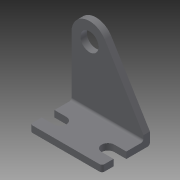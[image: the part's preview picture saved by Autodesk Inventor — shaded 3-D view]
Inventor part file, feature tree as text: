
AUTODESK INVENTOR PART (.ipt)
format: ipt  version: 2014 (Build 180170000, 170)  size: 189,440 bytes
history: native  units: in
note: dims shown in document units (in); Inventor stores cm internally (conversion verified against a paired STEP export)
features: other x147, sketch x8, extrude x5, hole x3
ambient origin geometry x8: Origin, YZ Plane, XZ Plane, XY Plane, X Axis, Y Axis, Z Axis, Center Point
bodies: Solid1 (feature_tree)
feature tree (163):
  extrude  "Extrusion1"  Depth=1.0in TaperAngle=0.0deg
  extrude  "Extrusion2"  Depth=0.1345in TaperAngle=0.0deg
  hole  "Hole1"  [1 undecoded]
  hole  "Hole2"  [1 undecoded]
  hole  "Hole3"  [1 undecoded]
  sketch  "Sketch_6"
  sketch  "Sketch_7"
  extrude  "Extrusion3"  [1 undecoded]
  extrude  "Extrusion4"  [1 undecoded]
  extrude  "Extrusion5"  [1 undecoded]
  other  "a1_XY"
  other  "a1_YZ"
  other  "a1_ZX"
  other  "a1_X"
  other  "a1_Y"
  other  "a1_Z"
  other  "a1_Center"
  other  "a2_XY"
  other  "a2_YZ"
  other  "a2_ZX"
  other  "a2_X"
  other  "a2_Y"
  other  "a2_Z"
  other  "a2_Center"
  other  "b1_XY"
  other  "b1_YZ"
  other  "b1_ZX"
  other  "b1_X"
  other  "b1_Y"
  other  "b1_Z"
  other  "b1_Center"
  other  "b2_XY"
  other  "b2_YZ"
  other  "b2_ZX"
  other  "b2_X"
  other  "b2_Y"
  other  "b2_Z"
  other  "b2_Center"
  other  "d1_XY"
  other  "d1_YZ"
  other  "d1_ZX"
  other  "d1_X"
  other  "d1_Y"
  other  "d1_Z"
  other  "d1_Center"
  other  "d2_XY"
  other  "d2_YZ"
  other  "d2_ZX"
  other  "d2_X"
  other  "d2_Y"
  other  "d2_Z"
  other  "d2_Center"
  other  "e1_XY"
  other  "e1_YZ"
  other  "e1_ZX"
  other  "e1_X"
  other  "e1_Y"
  other  "e1_Z"
  other  "e1_Center"
  other  "e2_XY"
  other  "e2_YZ"
  other  "e2_ZX"
  other  "e2_X"
  other  "e2_Y"
  other  "e2_Z"
  other  "e2_Center"
  other  "f1_XY"
  other  "f1_YZ"
  other  "f1_ZX"
  other  "f1_X"
  other  "f1_Y"
  other  "f1_Z"
  other  "f1_Center"
  other  "f2_XY"
  other  "f2_YZ"
  other  "f2_ZX"
  other  "f2_X"
  other  "f2_Y"
  other  "f2_Z"
  other  "f2_Center"
  other  "g1_XY"
  other  "g1_YZ"
  other  "g1_ZX"
  other  "g1_X"
  other  "g1_Y"
  other  "g1_Z"
  other  "g1_Center"
  other  "g2_XY"
  other  "g2_YZ"
  other  "g2_ZX"
  other  "g2_X"
  other  "g2_Y"
  other  "g2_Z"
  other  "g2_Center"
  other  "h1_XY"
  other  "h1_YZ"
  other  "h1_ZX"
  other  "h1_X"
  other  "h1_Y"
  other  "h1_Z"
  other  "h1_Center"
  other  "h2_XY"
  other  "h2_YZ"
  other  "h2_ZX"
  other  "h2_X"
  other  "h2_Y"
  other  "h2_Z"
  other  "h2_Center"
  other  "i_XY"
  other  "i_YZ"
  other  "i_ZX"
  other  "i_X"
  other  "i_Y"
  other  "i_Z"
  other  "i_Center"
  other  "j1_XY"
  other  "j1_YZ"
  other  "j1_ZX"
  other  "j1_X"
  other  "j1_Y"
  other  "j1_Z"
  other  "j1_Center"
  other  "j2_XY"
  other  "j2_YZ"
  other  "j2_ZX"
  other  "j2_X"
  other  "j2_Y"
  other  "j2_Z"
  other  "j2_Center"
  other  "k11_XY"
  other  "k11_YZ"
  other  "k11_ZX"
  other  "k11_X"
  other  "k11_Y"
  other  "k11_Z"
  other  "k11_Center"
  other  "k12_XY"
  other  "k12_YZ"
  other  "k12_ZX"
  other  "k12_X"
  other  "k12_Y"
  other  "k12_Z"
  other  "k12_Center"
  other  "to_dummy_L_XY"
  other  "to_dummy_L_YZ"
  other  "to_dummy_L_ZX"
  other  "to_dummy_L_X"
  other  "to_dummy_L_Y"
  other  "to_dummy_L_Z"
  other  "to_dummy_L_Center"
  other  "to_pin_L_XY"
  other  "to_pin_L_YZ"
  other  "to_pin_L_ZX"
  other  "to_pin_L_X"
  other  "to_pin_L_Y"
  other  "to_pin_L_Z"
  other  "to_pin_L_Center"
  sketch  "Sketch_1"  dims[d0=1.5in d1=0.0in d2=1.0in d3=0.0in]
  sketch  "Sketch_2"  dims[d4=0.3775in d5=0.75in d6=0.375in d7=0.25in d8=0.5635in d9=0.1345in d10=0.0in]
  sketch  "Sketch3"  dims[d11=0.266in d12=0.75in d13=0.375in d14=0.25in d15=0.5635in d16=0.1345in d17=0.0in]
  sketch  "Sketch4"  dims[d18=0.266in d19=0.75in d20=0.375in d21=0.25in d22=0.5635in d23=0.1345in d24=0.0in d25=0.1345in d26=0.0in]
  sketch  "Sketch5"  dims[d27=0.1345in d28=0.0in d29=0.1345in d30=0.0in]
  sketch  "Sketch_8"
note: 6 required parameter values undecoded (feature->parameter linkage not recoverable at this tier; creation-order binding heuristic only, values carry confidence <= 0.55)
